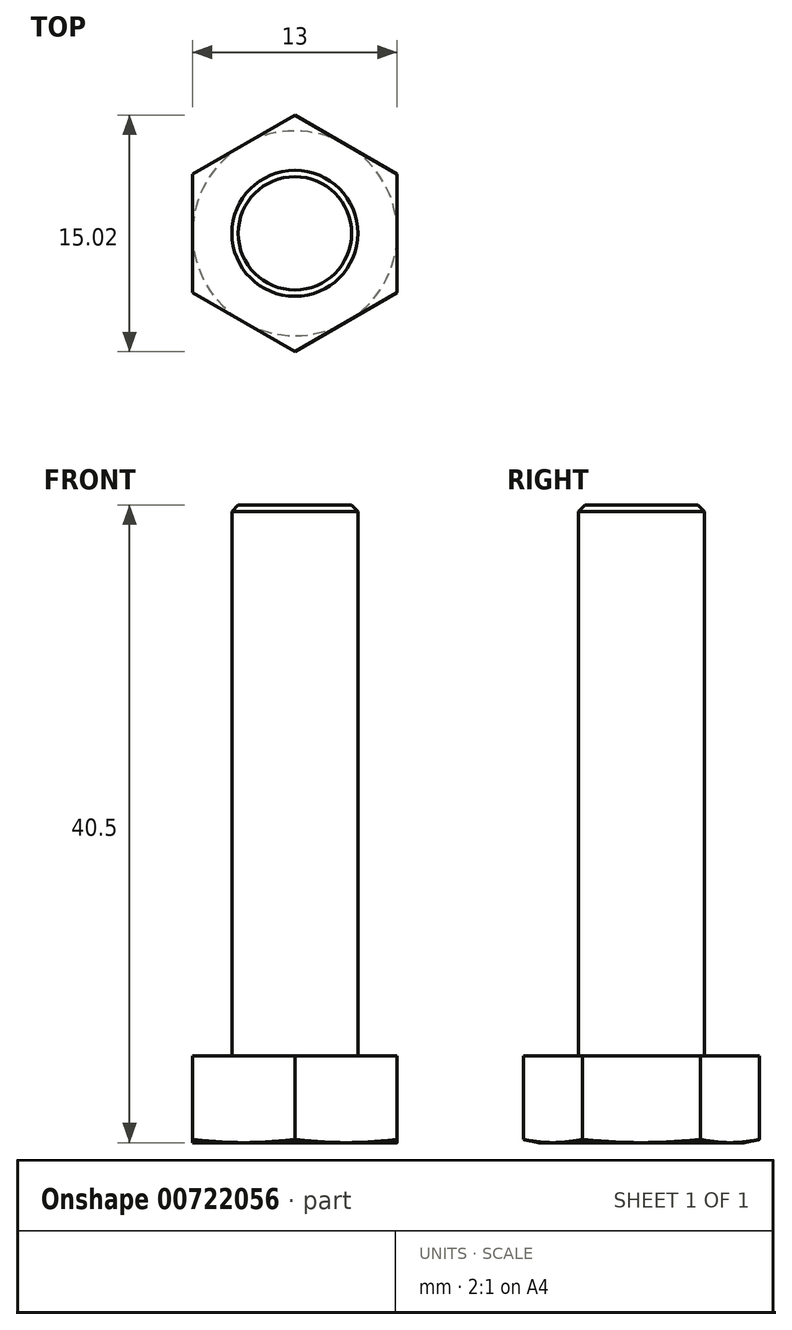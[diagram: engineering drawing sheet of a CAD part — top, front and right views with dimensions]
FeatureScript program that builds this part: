
annotation { "Feature Type Name" : "Feature", "Feature Type Description" : "" }
export const myFeature = defineFeature(function(context is Context, id is Id, definition is map)
    precondition{}
    {
        {
            var Q0;
            Q0=qCreatedBy(makeId("Top.planeOp"),FACE);
            var sketch = newSketch(context, id + "F0", { "sketchPlane" : qUnion([Q0])});
            skCircle(sketch, "E0.cCircle", {"center": v(0, 0) * mm, "radius": 6.5 * mm, "construction": true});
            skLineSegment(sketch, "E0.0", {"start": v(0, 7.5) * mm, "end": v(6.5, 3.75) * mm});
            skLineSegment(sketch, "E0.1", {"start": v(6.5, 3.75) * mm, "end": v(6.5, -3.75) * mm});
            skLineSegment(sketch, "E0.2", {"start": v(6.5, -3.75) * mm, "end": v(0, -7.5) * mm});
            skLineSegment(sketch, "E0.3", {"start": v(0, -7.5) * mm, "end": v(-6.5, -3.75) * mm});
            skLineSegment(sketch, "E0.4", {"start": v(-6.5, -3.75) * mm, "end": v(-6.5, 3.75) * mm});
            skLineSegment(sketch, "E0.5", {"start": v(-6.5, 3.75) * mm, "end": v(0, 7.5) * mm});
            skPoint(sketch, "E0.0.midPoint", {"position": v(3.25, 5.63) * mm});
            skSolve(sketch);
        }
        {
            var Q0;
            Q0=makeQuery(id+"F0.imprint","IMPRINT",FACE,{"disambiguationData":[TD([[makeQuery(id+"F0.imprint","IMPRINT",EDGE,{"derivedFrom":sQuery(id+"F0.wireOp",EDGE,"E0.0")}),-1.0]])]});
            extrude(context, id + "F1", {"entities" : qUnion([Q0]), "depth" : 5.5 * mm});
        }
        {
            var Q0;
            Q0=makeQuery(id+"F1.opExtrude","CAP_FACE",FACE,{"disambiguationData":[OSD([sQuery(id+"F0.wireOp",EDGE,"E0.0"),sQuery(id+"F0.wireOp",EDGE,"E0.1"),sQuery(id+"F0.wireOp",EDGE,"E0.2"),sQuery(id+"F0.wireOp",EDGE,"E0.3"),sQuery(id+"F0.wireOp",EDGE,"E0.4"),sQuery(id+"F0.wireOp",EDGE,"E0.5")])],"isStart":false});
            var sketch = newSketch(context, id + "F2", { "sketchPlane" : qUnion([Q0])});
            skCircle(sketch, "E1", {"center": v(0, 0) * mm, "radius": 4 * mm});
            skSolve(sketch);
        }
        {
            var Q0;
            Q0=makeQuery(id+"F2.imprint","IMPRINT",FACE,{"disambiguationData":[TD([[makeQuery(id+"F2.imprint","IMPRINT",EDGE,{"derivedFrom":sQuery(id+"F2.wireOp",EDGE,"E1")}),1.0]])]});
            extrude(context, id + "F3", {"entities" : qUnion([Q0]), "operationType" : NewBodyOperationType.ADD, "depth" : 35 * mm, "offsetDistance" : 25 * mm});
        }
        {
            var Q0;
            Q0=makeQuery(id+"F3.opExtrude","CAP_EDGE",EDGE,{"disambiguationData":[OSD([sQuery(id+"F2.wireOp",EDGE,"E1")])],"isStart":false});
            chamfer(context, id + "F4", {"entities" : qUnion([Q0]), "width" : 0.4 * mm, "tangentPropagation" : true});
        }
        {
            var Q0;
            Q0=qCreatedBy(makeId("Front.planeOp"),FACE);
            var sketch = newSketch(context, id + "F5", { "sketchPlane" : qUnion([Q0])});
            skLineSegment(sketch, "E2", {"start": v(-11.5, 0) * mm, "end": v(-6.5, 0) * mm});
            skLineSegment(sketch, "E3", {"start": v(-6.5, 0) * mm, "end": v(-11.5, 1) * mm});
            skLineSegment(sketch, "E4", {"start": v(-11.5, 1) * mm, "end": v(-11.5, 0) * mm});
            skSolve(sketch);
        }
        {
            var Q0;
            Q0=qSketchRegion(id+"F5",true);
            var Q1;
            Q1=makeQuery(id+"F5.imprint","IMPRINT",FACE,{"disambiguationData":[TD([[makeQuery(id+"F5.imprint","IMPRINT",EDGE,{"derivedFrom":sQuery(id+"F5.wireOp",EDGE,"E2")}),1.0]])]});
            var Q2;
            Q2=makeQuery(id+"F3.opExtrude","SWEPT_FACE",FACE,{"disambiguationData":[OSD([sQuery(id+"F2.wireOp",EDGE,"E1")])]});
            revolve(context, id + "F6", {"operationType" : NewBodyOperationType.REMOVE, "entities" : qUnion([Q0, Q1]), "axis" : qUnion([Q2]), "revolveType" : RevolveType.FULL, "oppositeDirection" : true});
        }
    });
